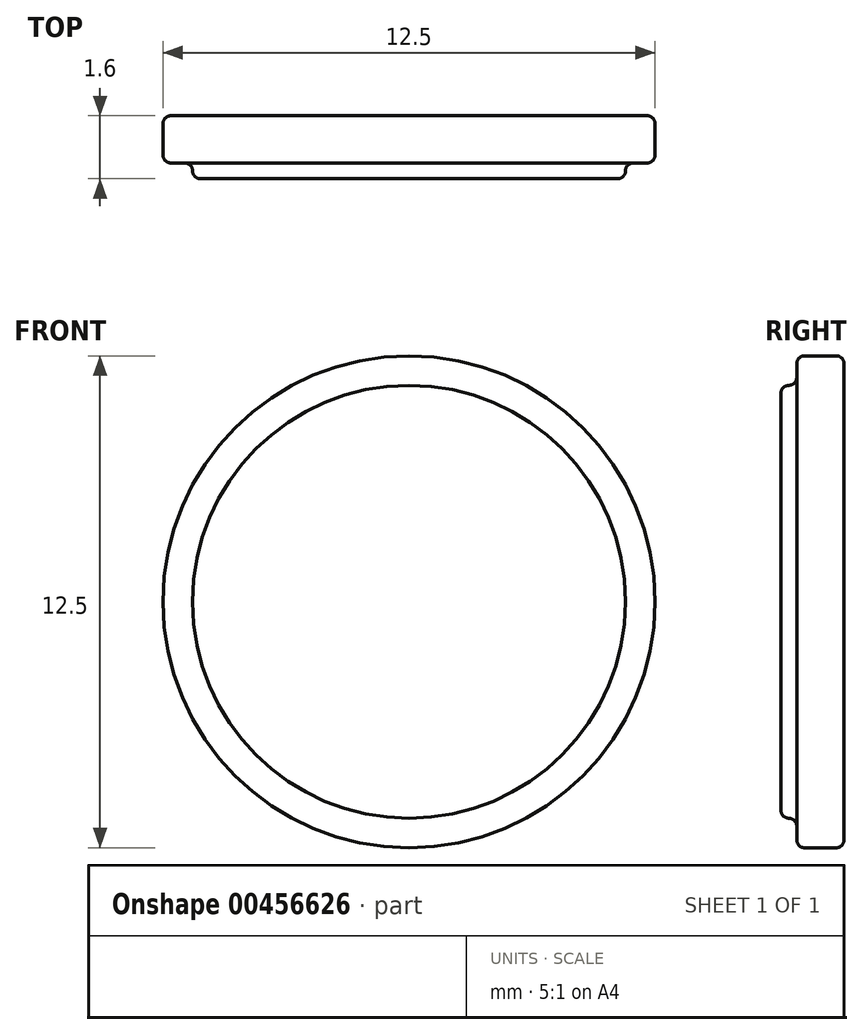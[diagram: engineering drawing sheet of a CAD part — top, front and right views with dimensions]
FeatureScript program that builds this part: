
annotation { "Feature Type Name" : "Feature", "Feature Type Description" : "" }
export const myFeature = defineFeature(function(context is Context, id is Id, definition is map)
    precondition{}
    {
        {
            var Q0;
            Q0=qCreatedBy(makeId("Front.planeOp"),FACE);
            var sketch = newSketch(context, id + "F0", { "sketchPlane" : qUnion([Q0])});
            skCircle(sketch, "E0", {"center": v(6.25, 6.25) * mm, "radius": 6.25 * mm});
            skCircle(sketch, "E1", {"center": v(6.25, 6.25) * mm, "radius": 5.5 * mm});
            skSolve(sketch);
        }
        {
            var Q0;
            Q0=makeQuery(id+"F0.imprint","IMPRINT",FACE,{"disambiguationData":[TD([[makeQuery(id+"F0.imprint","IMPRINT",EDGE,{"derivedFrom":sQuery(id+"F0.wireOp",EDGE,"E1")}),1.0]])]});
            extrude(context, id + "F1", {"entities" : qUnion([Q0]), "depth" : 1.6 * mm});
        }
        {
            var Q0;
            Q0=makeQuery(id+"F0.imprint","IMPRINT",FACE,{"disambiguationData":[TD([[makeQuery(id+"F0.imprint","IMPRINT",EDGE,{"derivedFrom":sQuery(id+"F0.wireOp",EDGE,"E0")}),1.0]])]});
            extrude(context, id + "F2", {"entities" : qUnion([Q0]), "operationType" : NewBodyOperationType.ADD, "depth" : 1.2 * mm});
        }
        {
            var Q0;
            Q0=makeQuery(id+"F1.opExtrude","CAP_FACE",FACE,{"disambiguationData":[OSD([sQuery(id+"F0.wireOp",EDGE,"E1")])],"isStart":false});
            var Q1;
            Q1=makeQuery(id+"F2.opExtrude","SWEPT_FACE",FACE,{"disambiguationData":[OSD([sQuery(id+"F0.wireOp",EDGE,"E0")])]});
            var Q2;
            Q2=makeQuery(id+"F2.opExtrude","CAP_FACE",FACE,{"disambiguationData":[OSD([sQuery(id+"F0.wireOp",EDGE,"E0"),sQuery(id+"F0.wireOp",EDGE,"E1")])],"isStart":false});
            var Q3;
            Q3=makeQuery(id+"F1.opExtrude","SWEPT_FACE",FACE,{"disambiguationData":[OSD([sQuery(id+"F0.wireOp",EDGE,"E1")])]});
            fillet(context, id + "F3", {"entities" : qUnion([Q0, Q1, Q2, Q3]), "radius" : .2 * mm, "tangentPropagation" : true, "allowEdgeOverflow" : false});
        }
    });
